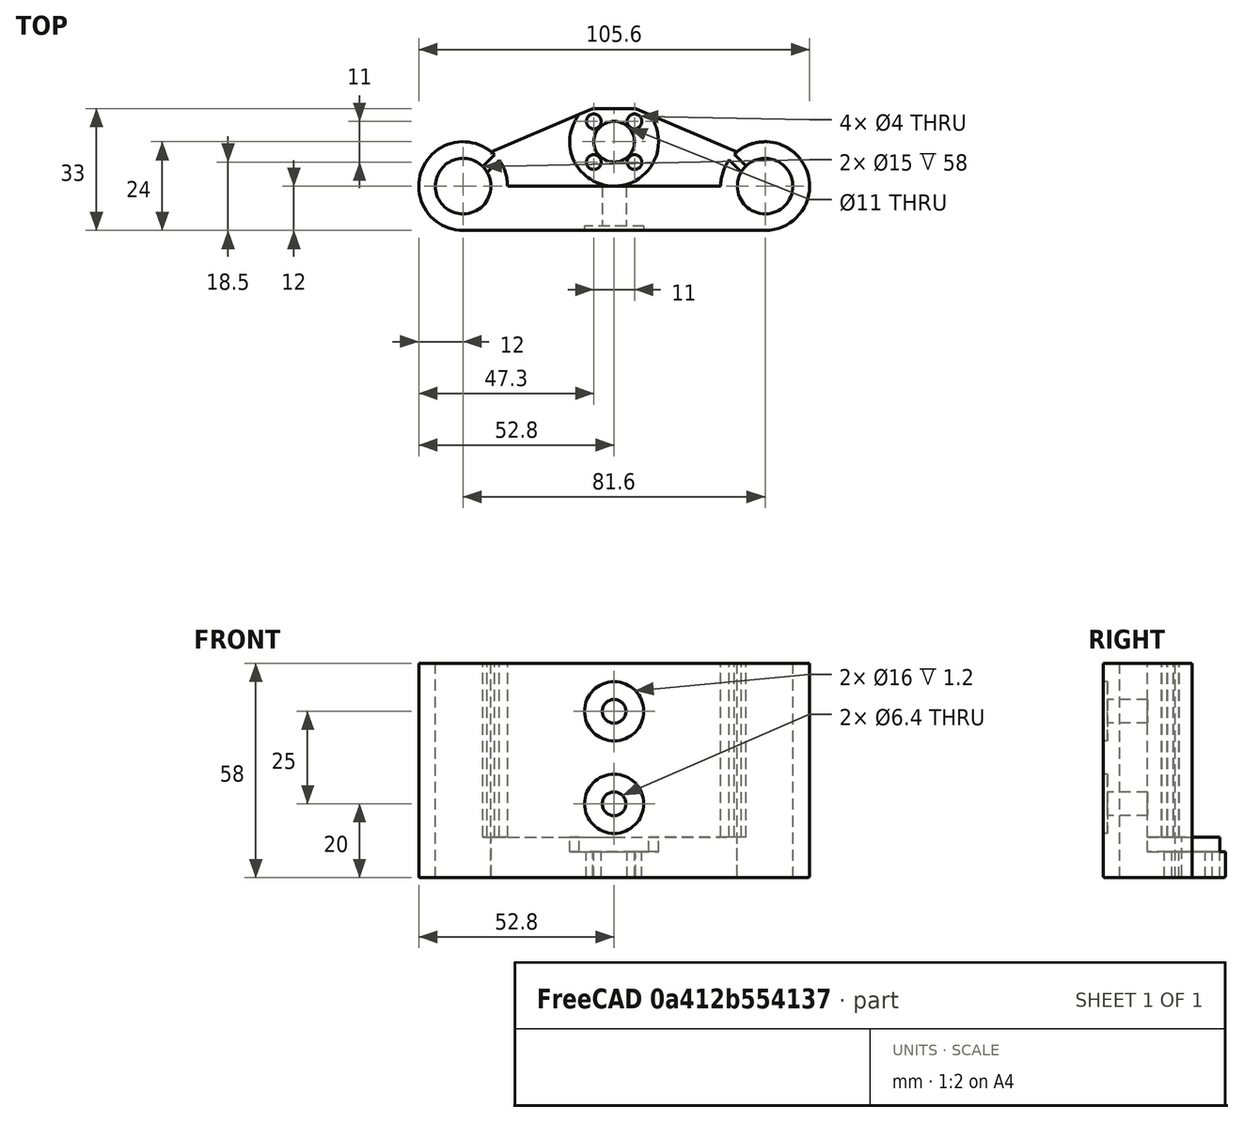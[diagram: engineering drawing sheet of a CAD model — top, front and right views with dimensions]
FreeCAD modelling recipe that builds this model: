
FCSTD DOCUMENT  (FreeCAD 0.18R16146 (Git))
Label: Y_Schlitten_Ver4
License: All rights reserved
LicenseURL: http://en.wikipedia.org/wiki/All_rights_reserved
objects: Part::Cylinder×14, Part::Cut×14, Part::Box×4, Part::Chamfer×1, Part::MultiFuse×1, Part::Fillet×1
note: 35 computed .brp shape members not serialized (recipe doc carries the construction recipe); baked Part::Feature solids carry a one-line shape summary decoded from their .brp

FEATURE [Part::Cylinder] Cylinder  label="Zylinder"
  Angle = 360
  AttacherType = Attacher::AttachEngine3D
  Height = 58
  Radius = 7.5
FEATURE [Part::Cylinder] Cylinder001  label="Zylinder001"
  Angle = 360
  AttacherType = Attacher::AttachEngine3D
  Height = 58
  Radius = 12
FEATURE [Part::Cylinder] Cylinder002  label="Zylinder002"
  Angle = 360
  AttacherType = Attacher::AttachEngine3D
  Height = 58
  Placement = pos=(81.6,0,0) rot=(0,0,1;0rad)
  Radius = 7.5
FEATURE [Part::Cylinder] Cylinder003  label="Zylinder003"
  Angle = 360
  AttacherType = Attacher::AttachEngine3D
  Height = 58
  Placement = pos=(81.6,0,0) rot=(0,0,1;0rad)
  Radius = 12
FEATURE [Part::Box] Box  label="Würfel"
  AttacherType = Attacher::AttachEngine3D
  Height = 58
  Length = 81.6
  Placement = pos=(0,-12,0) rot=(0,0,1;0rad)
  Width = 12
FEATURE [Part::Cylinder] Cylinder004  label="Zylinder004"
  Angle = 360
  AttacherType = Attacher::AttachEngine3D
  Height = 20
  Placement = pos=(40.8,12,0) rot=(0,0,1;0rad)
  Radius = 5.5
FEATURE [Part::Cylinder] Cylinder005  label="Zylinder005"
  Angle = 360
  AttacherType = Attacher::AttachEngine3D
  Height = 4
  Placement = pos=(40.8,12,7) rot=(0,0,1;0rad)
  Radius = 12
FEATURE [Part::Cylinder] Cylinder006  label="Zylinder006"
  Angle = 360
  AttacherType = Attacher::AttachEngine3D
  Height = 20
  Placement = pos=(35.3,6.5,0) rot=(0,0,1;0rad)
  Radius = 2
FEATURE [Part::Cylinder] Cylinder007  label="Zylinder007"
  Angle = 360
  AttacherType = Attacher::AttachEngine3D
  Height = 20
  Placement = pos=(35.3,17.5,0) rot=(0,0,1;0rad)
  Radius = 2
FEATURE [Part::Cylinder] Cylinder008  label="Zylinder008"
  Angle = 360
  AttacherType = Attacher::AttachEngine3D
  Height = 20
  Placement = pos=(46.3,6.5,0) rot=(0,0,1;0rad)
  Radius = 2
FEATURE [Part::Cylinder] Cylinder009  label="Zylinder009"
  Angle = 360
  AttacherType = Attacher::AttachEngine3D
  Height = 20
  Placement = pos=(46.3,17.5,0) rot=(0,0,1;0rad)
  Radius = 2
FEATURE [Part::Box] Box001  label="Würfel001"
  AttacherType = Attacher::AttachEngine3D
  Height = 11
  Length = 81.6
  Placement = pos=(0,-12,0) rot=(0,0,1;0rad)
  Width = 33
FEATURE [Part::Chamfer] Chamfer
  Base = -> Box001
  Edges = 2 edges: [Edge3 r1=15 r2=35,Edge7 r1=15 r2=35]
FEATURE [Part::MultiFuse] Fusion
  Shapes = -> [Box,Chamfer,Cylinder001,Cylinder003]
FEATURE [Part::Cut] Cut
  Base = -> Fusion
  Tool = -> Cylinder
FEATURE [Part::Cut] Cut001
  Base = -> Cut
  Tool = -> Cylinder002
FEATURE [Part::Cut] Cut002
  Base = -> Cut001
  Tool = -> Cylinder004
FEATURE [Part::Box] Box002  label="Würfel002"
  AttacherType = Attacher::AttachEngine3D
  Height = 60
  Length = 2
  Placement = pos=(77,2,11) rot=(0,0,1;0.785398rad)
  Width = 10
FEATURE [Part::Cut] Cut003
  Base = -> Cut002
  Tool = -> Cylinder005
FEATURE [Part::Cut] Cut004
  Base = -> Cut003
  Tool = -> Cylinder009
FEATURE [Part::Cut] Cut005
  Base = -> Cut004
  Tool = -> Cylinder008
FEATURE [Part::Cut] Cut006
  Base = -> Cut005
  Tool = -> Cylinder007
FEATURE [Part::Cut] Cut007
  Base = -> Cut006
  Tool = -> Cylinder006
FEATURE [Part::Cylinder] Cylinder010  label="Cylinder"
  Angle = 360
  AttacherType = Attacher::AttachEngine3D
  Height = 40
  Placement = pos=(40.8,20,20) rot=(1,0,0;1.5708rad)
  Radius = 3.2
FEATURE [Part::Cylinder] Cylinder011  label="Cylinder001"
  Angle = 360
  AttacherType = Attacher::AttachEngine3D
  Height = 40
  Placement = pos=(40.8,20,45) rot=(1,0,0;1.5708rad)
  Radius = 3.2
FEATURE [Part::Box] Box003  label="Würfel003"
  AttacherType = Attacher::AttachEngine3D
  Height = 60
  Length = 2
  Placement = pos=(3,3,11) rot=(0,0,-1;0.785398rad)
  Width = 10
FEATURE [Part::Cut] Cut008
  Base = -> Cut007
  Tool = -> Box003
FEATURE [Part::Cut] Cut009
  Base = -> Cut008
  Tool = -> Box002
FEATURE [Part::Cylinder] Cylinder012  label="Cylinder002"
  Angle = 360
  AttacherType = Attacher::AttachEngine3D
  Height = 1.2
  Placement = pos=(40.8,-10.8,20) rot=(1,0,0;1.5708rad)
  Radius = 8
FEATURE [Part::Cylinder] Cylinder013  label="Cylinder003"
  Angle = 360
  AttacherType = Attacher::AttachEngine3D
  Height = 1.2
  Placement = pos=(40.8,-10.8,45) rot=(1,0,0;1.5708rad)
  Radius = 8
FEATURE [Part::Cut] Cut010
  Base = -> Cut009
  Tool = -> Cylinder013
FEATURE [Part::Cut] Cut011
  Base = -> Cut010
  Tool = -> Cylinder012
FEATURE [Part::Cut] Cut012
  Base = -> Cut011
  Tool = -> Cylinder011
FEATURE [Part::Cut] Cut013
  Base = -> Cut012
  Tool = -> Cylinder010
FEATURE [Part::Fillet] Fillet
  Base = -> Cut013
  Edges = 7 edges r=0.5: [Edge7,Edge19,Edge36,Edge38,Edge39,Edge97,Edge98]
